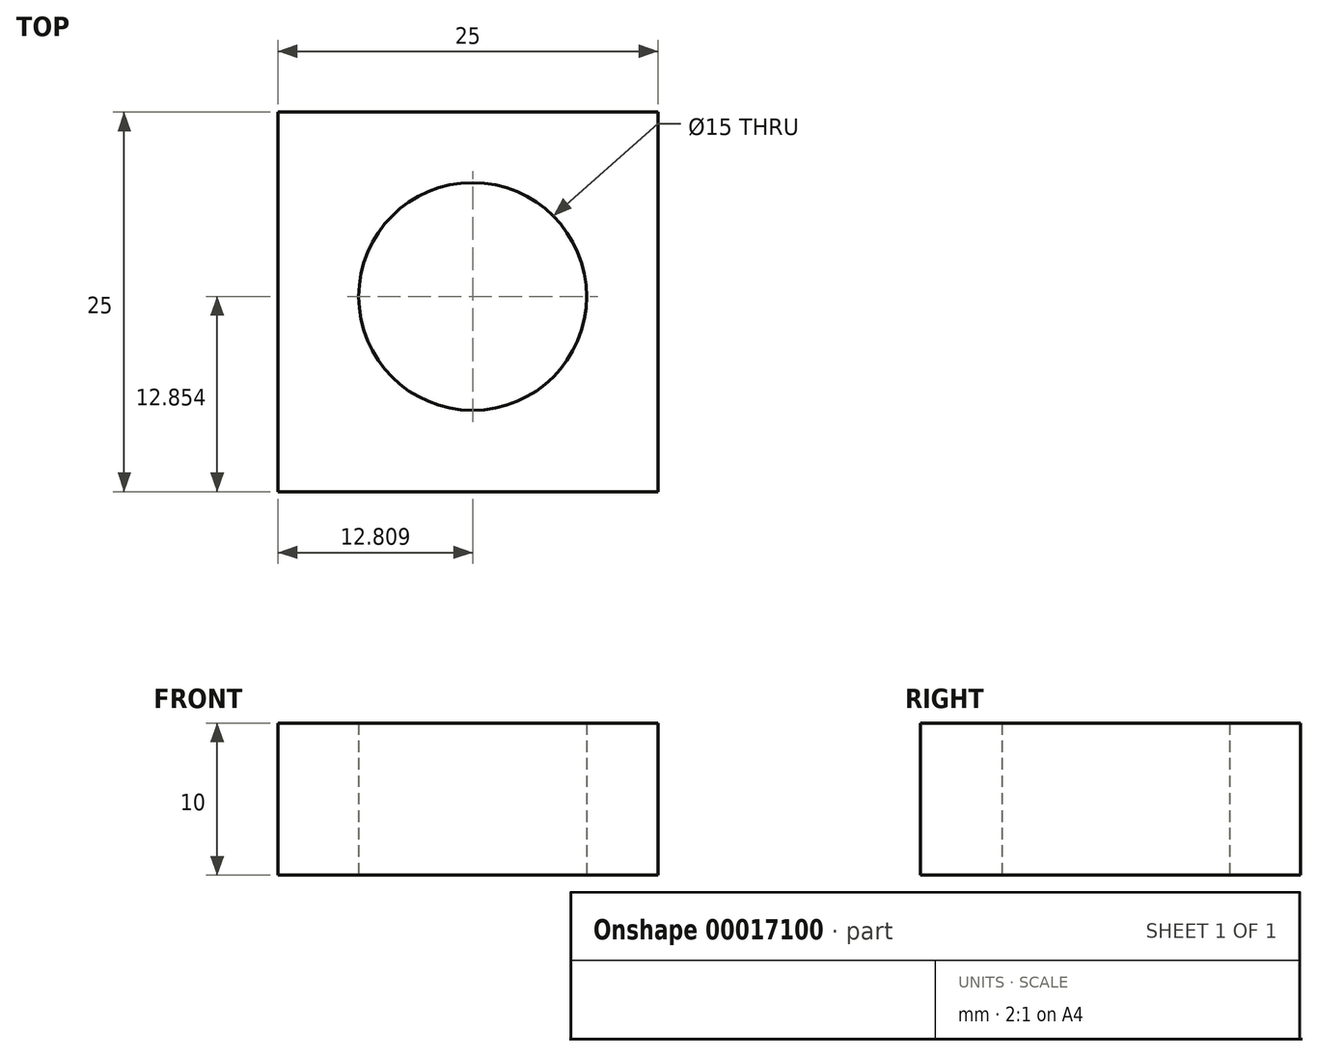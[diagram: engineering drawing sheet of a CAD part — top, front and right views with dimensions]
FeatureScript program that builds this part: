
annotation { "Feature Type Name" : "Feature", "Feature Type Description" : "" }
export const myFeature = defineFeature(function(context is Context, id is Id, definition is map)
    precondition{}
    {
        {
            var Q0;
            Q0=qCreatedBy(makeId("Top.planeOp"),FACE);
            var sketch = newSketch(context, id + "F0", { "sketchPlane" : qUnion([Q0])});
            skLineSegment(sketch, "E0.bottom", {"start": v(-14.95, 2.02) * mm, "end": v(10.05, 2.02) * mm});
            skLineSegment(sketch, "E0.top", {"start": v(-14.95, -22.98) * mm, "end": v(10.05, -22.98) * mm});
            skLineSegment(sketch, "E0.left", {"start": v(-14.95, 2.02) * mm, "end": v(-14.95, -22.98) * mm});
            skLineSegment(sketch, "E0.right", {"start": v(10.05, 2.02) * mm, "end": v(10.05, -22.98) * mm});
            skCircle(sketch, "E1", {"center": v(-2.14, -10.13) * mm, "radius": 7.5 * mm});
            skSolve(sketch);
        }
        {
            var Q0;
            Q0=makeQuery(id+"F0.imprint","IMPRINT",FACE,{"disambiguationData":[TD([[makeQuery(id+"F0.imprint","IMPRINT",EDGE,{"derivedFrom":sQuery(id+"F0.wireOp",EDGE,"E0.bottom")}),-1.0]])]});
            extrude(context, id + "F1", {"entities" : qUnion([Q0]), "depth" : 10 * mm});
        }
    });
